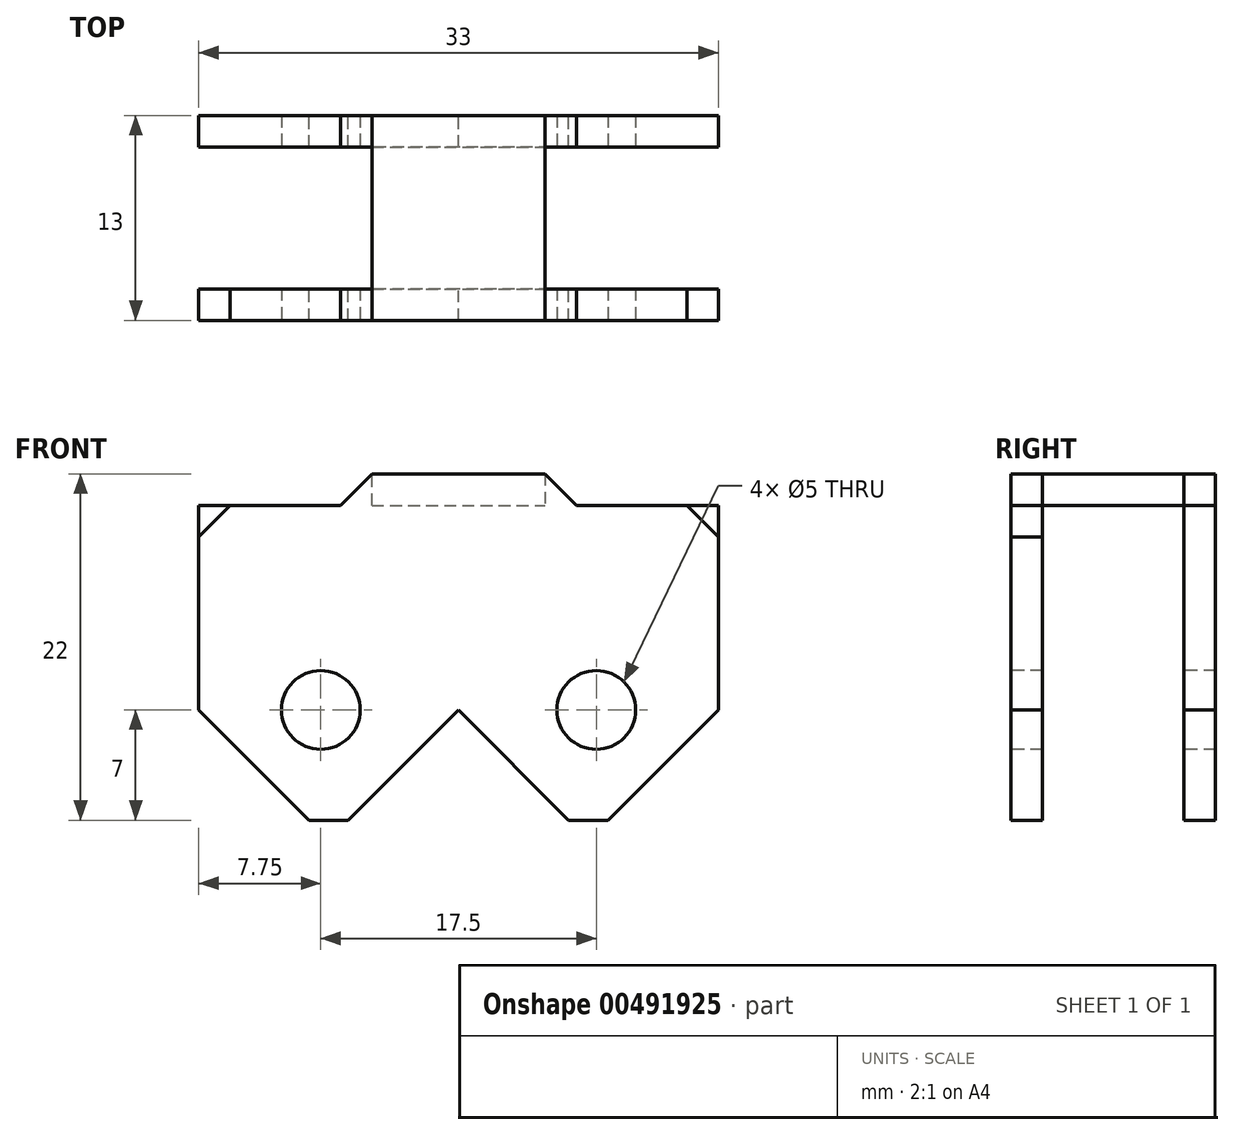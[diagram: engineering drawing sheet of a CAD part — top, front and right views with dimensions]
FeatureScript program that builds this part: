
annotation { "Feature Type Name" : "Feature", "Feature Type Description" : "" }
export const myFeature = defineFeature(function(context is Context, id is Id, definition is map)
    precondition{}
    {
        {
            var Q0;
            Q0=qCreatedBy(makeId("Front.planeOp"),FACE);
            var sketch = newSketch(context, id + "F0", { "sketchPlane" : qUnion([Q0])});
            skLineSegment(sketch, "E0.bottom", {"start": v(-16.5, 11) * mm, "end": v(16.5, 11) * mm});
            skLineSegment(sketch, "E0.top", {"start": v(-16.5, -11) * mm, "end": v(16.5, -11) * mm});
            skLineSegment(sketch, "E0.left", {"start": v(-16.5, 11) * mm, "end": v(-16.5, -11) * mm});
            skLineSegment(sketch, "E0.right", {"start": v(16.5, 11) * mm, "end": v(16.5, -11) * mm});
            skPoint(sketch, "E0.middle", {"position": v(0, 0) * mm});
            skSolve(sketch);
        }
        {
            assignVariable(context, id + "F1", {"name" : "depth", "anyValue" : 13});
        }
        {
            var Q0;
            Q0=makeQuery(id+"F0.imprint","IMPRINT",FACE,{"disambiguationData":[TD([[makeQuery(id+"F0.imprint","IMPRINT",EDGE,{"derivedFrom":sQuery(id+"F0.wireOp",EDGE,"E0.bottom")}),-1.0]])]});
            extrude(context, id + "F2", {"entities" : qUnion([Q0]), "depth" : (getVariable(context, 'depth')) * mm});
        }
        {
            var Q0;
            Q0=makeQuery(id+"F2.opExtrude","SWEPT_EDGE",EDGE,{"disambiguationData":[OSD([sQuery(id+"F0.wireOp",EDGE,"E0.top"),sQuery(id+"F0.wireOp",EDGE,"E0.left")])]});
            var Q1;
            Q1=makeQuery(id+"F2.opExtrude","SWEPT_EDGE",EDGE,{"disambiguationData":[OSD([sQuery(id+"F0.wireOp",EDGE,"E0.top"),sQuery(id+"F0.wireOp",EDGE,"E0.right")])]});
            chamfer(context, id + "F3", {"entities" : qUnion([Q0, Q1]), "width" : 7 * mm, "tangentPropagation" : true});
        }
        {
            var Q0;
            Q0=makeQuery(id+"F2.opExtrude","CAP_FACE",FACE,{"disambiguationData":[OSD([sQuery(id+"F0.wireOp",EDGE,"E0.bottom"),sQuery(id+"F0.wireOp",EDGE,"E0.top"),sQuery(id+"F0.wireOp",EDGE,"E0.left"),sQuery(id+"F0.wireOp",EDGE,"E0.right")])],"isStart":false});
            var sketch = newSketch(context, id + "F4", { "sketchPlane" : qUnion([Q0])});
            skCircle(sketch, "E1", {"center": v(-8.75, -4) * mm, "radius": 2.5 * mm});
            skCircle(sketch, "E2", {"center": v(8.75, -4) * mm, "radius": 2.5 * mm});
            skSolve(sketch);
        }
        {
            var Q0;
            Q0=makeQuery(id+"F4.imprint","IMPRINT",FACE,{"disambiguationData":[TD([[makeQuery(id+"F4.imprint","IMPRINT",EDGE,{"derivedFrom":sQuery(id+"F4.wireOp",EDGE,"E1")}),1.0]])]});
            var Q1;
            Q1=makeQuery(id+"F4.imprint","IMPRINT",FACE,{"disambiguationData":[TD([[makeQuery(id+"F4.imprint","IMPRINT",EDGE,{"derivedFrom":sQuery(id+"F4.wireOp",EDGE,"E2")}),1.0]])]});
            extrude(context, id + "F5", {"entities" : qUnion([Q0, Q1]), "operationType" : NewBodyOperationType.REMOVE, "oppositeDirection" : true, "depth" : 25 * mm});
        }
        {
            var Q0;
            Q0=makeQuery(id+"F2.opExtrude","SWEPT_FACE",FACE,{"disambiguationData":[OSD([sQuery(id+"F0.wireOp",EDGE,"E0.top")])]});
            var Q1;
            Q1=makeQuery(id+"F3.opChamfer","BLEND_FACE",FACE,{"disambiguationData":[OSD([sQuery(id+"F0.wireOp",EDGE,"E0.top"),sQuery(id+"F0.wireOp",EDGE,"E0.right")])]});
            var Q2;
            Q2=makeQuery(id+"F2.opExtrude","SWEPT_FACE",FACE,{"disambiguationData":[OSD([sQuery(id+"F0.wireOp",EDGE,"E0.right")])]});
            var Q3;
            Q3=makeQuery(id+"F2.opExtrude","SWEPT_FACE",FACE,{"disambiguationData":[OSD([sQuery(id+"F0.wireOp",EDGE,"E0.left")])]});
            var Q4;
            Q4=makeQuery(id+"F3.opChamfer","BLEND_FACE",FACE,{"disambiguationData":[OSD([sQuery(id+"F0.wireOp",EDGE,"E0.top"),sQuery(id+"F0.wireOp",EDGE,"E0.left")])]});
            var Q5;
            Q5=makeQuery(id+"F5.boolean.opBoolean","COPY",FACE,{"derivedFrom":makeQuery(id+"F5.opExtrude","SWEPT_FACE",FACE,{"disambiguationData":[OSD([sQuery(id+"F4.wireOp",EDGE,"E1")])]})});
            var Q6;
            Q6=makeQuery(id+"F5.boolean.opBoolean","COPY",FACE,{"derivedFrom":makeQuery(id+"F5.opExtrude","SWEPT_FACE",FACE,{"disambiguationData":[OSD([sQuery(id+"F4.wireOp",EDGE,"E2")])]})});
            shell(context, id + "F6", {"entities" : qUnion([Q0, Q1, Q2, Q3, Q4, Q5, Q6]), "thickness" : 2 * mm});
        }
        {
            var Q0;
            Q0=makeQuery(id+"F2.opExtrude","SWEPT_FACE",FACE,{"disambiguationData":[OSD([sQuery(id+"F0.wireOp",EDGE,"E0.bottom")])]});
            var sketch = newSketch(context, id + "F7", { "sketchPlane" : qUnion([Q0])});
            skLineSegment(sketch, "E3.bottom", {"start": v(16.5, -13) * mm, "end": v(5.5, -13) * mm});
            skLineSegment(sketch, "E3.top", {"start": v(16.5, 0) * mm, "end": v(5.5, 0) * mm});
            skLineSegment(sketch, "E3.left", {"start": v(16.5, -13) * mm, "end": v(16.5, 0) * mm});
            skLineSegment(sketch, "E3.right", {"start": v(5.5, -13) * mm, "end": v(5.5, 0) * mm});
            skLineSegment(sketch, "E4.bottom", {"start": v(-16.5, -13) * mm, "end": v(-5.5, -13) * mm});
            skLineSegment(sketch, "E4.top", {"start": v(-16.5, 0) * mm, "end": v(-5.5, 0) * mm});
            skLineSegment(sketch, "E4.left", {"start": v(-16.5, -13) * mm, "end": v(-16.5, 0) * mm});
            skLineSegment(sketch, "E4.right", {"start": v(-5.5, -13) * mm, "end": v(-5.5, 0) * mm});
            skSolve(sketch);
        }
        {
            var Q0;
            Q0=makeQuery(id+"F7.imprint","IMPRINT",FACE,{"disambiguationData":[TD([[makeQuery(id+"F7.imprint","IMPRINT",EDGE,{"derivedFrom":sQuery(id+"F7.wireOp",EDGE,"E3.bottom")}),1.0]])]});
            var Q1;
            Q1=makeQuery(id+"F7.imprint","IMPRINT",FACE,{"disambiguationData":[TD([[makeQuery(id+"F7.imprint","IMPRINT",EDGE,{"derivedFrom":sQuery(id+"F7.wireOp",EDGE,"E4.bottom")}),1.0]])]});
            extrude(context, id + "F8", {"entities" : qUnion([Q0, Q1]), "operationType" : NewBodyOperationType.REMOVE, "oppositeDirection" : true, "depth" : 2 * mm});
        }
        {
            var Q0;
            {var subQ0=sQuery(id+"F7.wireOp",EDGE,"E3.right");Q0=makeQuery(id+"F8.boolean.opBoolean","COPY",EDGE,{"disambiguationData":[topologyDisambiguationEdgeConnected([makeQuery(id+"F6.opShell","OFFSET_FACE",FACE,{"disambiguationData":[OSD([sQuery(id+"F0.wireOp",EDGE,"E0.bottom")])]}),makeQuery(id+"F8.opExtrude","SWEPT_FACE",FACE,{"disambiguationData":[OSD([subQ0])]})])],"derivedFrom":makeQuery(id+"F8.opExtrude","CAP_EDGE",EDGE,{"disambiguationData":[OSD([subQ0])],"isStart":false})});}
            var Q1;
            {var subQ0=sQuery(id+"F7.wireOp",EDGE,"E4.right");Q1=makeQuery(id+"F8.boolean.opBoolean","COPY",EDGE,{"disambiguationData":[topologyDisambiguationEdgeConnected([makeQuery(id+"F6.opShell","OFFSET_FACE",FACE,{"disambiguationData":[OSD([sQuery(id+"F0.wireOp",EDGE,"E0.bottom")])]}),makeQuery(id+"F8.opExtrude","SWEPT_FACE",FACE,{"disambiguationData":[OSD([subQ0])]})])],"derivedFrom":makeQuery(id+"F8.opExtrude","CAP_EDGE",EDGE,{"disambiguationData":[OSD([subQ0])],"isStart":false})});}
            chamfer(context, id + "F9", {"entities" : qUnion([Q0, Q1]), "width" : 2 * mm, "tangentPropagation" : true});
        }
        {
            var Q0;
            Q0=makeQuery(id+"F2.opExtrude","CAP_FACE",FACE,{"disambiguationData":[OSD([sQuery(id+"F0.wireOp",EDGE,"E0.bottom"),sQuery(id+"F0.wireOp",EDGE,"E0.top"),sQuery(id+"F0.wireOp",EDGE,"E0.left"),sQuery(id+"F0.wireOp",EDGE,"E0.right")])],"isStart":true});
            var sketch = newSketch(context, id + "F10", { "sketchPlane" : qUnion([Q0])});
            skLineSegment(sketch, "E5", {"start": v(0, -4.01) * mm, "end": v(-7, -11) * mm});
            skLineSegment(sketch, "E6", {"start": v(-7, -11) * mm, "end": v(7, -11) * mm});
            skLineSegment(sketch, "E7", {"start": v(7, -11) * mm, "end": v(0, -4.01) * mm});
            skSolve(sketch);
        }
        {
            var Q0;
            Q0=makeQuery(id+"F10.imprint","IMPRINT",FACE,{"disambiguationData":[TD([[makeQuery(id+"F10.imprint","IMPRINT",EDGE,{"derivedFrom":sQuery(id+"F10.wireOp",EDGE,"E5")}),1.0]])]});
            extrude(context, id + "F11", {"entities" : qUnion([Q0]), "operationType" : NewBodyOperationType.REMOVE, "oppositeDirection" : true, "depth" : 25 * mm});
        }
        {
            var Q0;
            {var subQ0=sQuery(id+"F0.wireOp",EDGE,"E0.right");var subQ1=sQuery(id+"F0.wireOp",EDGE,"E0.left");var subQ2=sQuery(id+"F0.wireOp",EDGE,"E0.top");var subQ3=sQuery(id+"F0.wireOp",EDGE,"E0.bottom");var subQ4=makeQuery(id+"F2.opExtrude","CAP_FACE",FACE,{"disambiguationData":[OSD([subQ3,subQ2,subQ1,subQ0])],"isStart":false});var subQ5=sQuery(id+"F7.wireOp",EDGE,"E3.left");Q0=makeQuery(id+"F8.boolean.opBoolean","COPY",EDGE,{"disambiguationData":[TD([subQ4])],"derivedFrom":makeQuery(id+"F8.opExtrude","CAP_EDGE",EDGE,{"disambiguationData":[OSD([subQ5])],"isStart":false})});}
            var Q1;
            {var subQ0=sQuery(id+"F0.wireOp",EDGE,"E0.right");var subQ1=sQuery(id+"F0.wireOp",EDGE,"E0.left");var subQ2=sQuery(id+"F0.wireOp",EDGE,"E0.top");var subQ3=sQuery(id+"F0.wireOp",EDGE,"E0.bottom");var subQ4=makeQuery(id+"F2.opExtrude","CAP_FACE",FACE,{"disambiguationData":[OSD([subQ3,subQ2,subQ1,subQ0])],"isStart":true});var subQ5=sQuery(id+"F7.wireOp",EDGE,"E3.left");Q1=makeQuery(id+"F8.boolean.opBoolean","COPY",EDGE,{"disambiguationData":[TD([subQ4])],"derivedFrom":makeQuery(id+"F8.opExtrude","CAP_EDGE",EDGE,{"disambiguationData":[OSD([subQ5])],"isStart":false})});}
            var Q2;
            {var subQ0=sQuery(id+"F0.wireOp",EDGE,"E0.right");var subQ1=sQuery(id+"F0.wireOp",EDGE,"E0.left");var subQ2=sQuery(id+"F0.wireOp",EDGE,"E0.top");var subQ3=sQuery(id+"F0.wireOp",EDGE,"E0.bottom");var subQ4=makeQuery(id+"F2.opExtrude","CAP_FACE",FACE,{"disambiguationData":[OSD([subQ3,subQ2,subQ1,subQ0])],"isStart":false});var subQ5=sQuery(id+"F7.wireOp",EDGE,"E4.left");Q2=makeQuery(id+"F8.boolean.opBoolean","COPY",EDGE,{"disambiguationData":[TD([subQ4])],"derivedFrom":makeQuery(id+"F8.opExtrude","CAP_EDGE",EDGE,{"disambiguationData":[OSD([subQ5])],"isStart":false})});}
            var Q3;
            {var subQ0=sQuery(id+"F0.wireOp",EDGE,"E0.right");var subQ1=sQuery(id+"F0.wireOp",EDGE,"E0.left");var subQ2=sQuery(id+"F0.wireOp",EDGE,"E0.top");var subQ3=sQuery(id+"F0.wireOp",EDGE,"E0.bottom");var subQ4=makeQuery(id+"F2.opExtrude","CAP_FACE",FACE,{"disambiguationData":[OSD([subQ3,subQ2,subQ1,subQ0])],"isStart":true});var subQ5=sQuery(id+"F7.wireOp",EDGE,"E4.left");Q3=makeQuery(id+"F8.boolean.opBoolean","COPY",EDGE,{"disambiguationData":[TD([subQ4])],"derivedFrom":makeQuery(id+"F8.opExtrude","CAP_EDGE",EDGE,{"disambiguationData":[OSD([subQ5])],"isStart":false})});}
            chamfer(context, id + "F12", {"entities" : qUnion([Q0, Q1, Q2, Q3]), "width" : 2 * mm, "tangentPropagation" : true});
        }
    });
